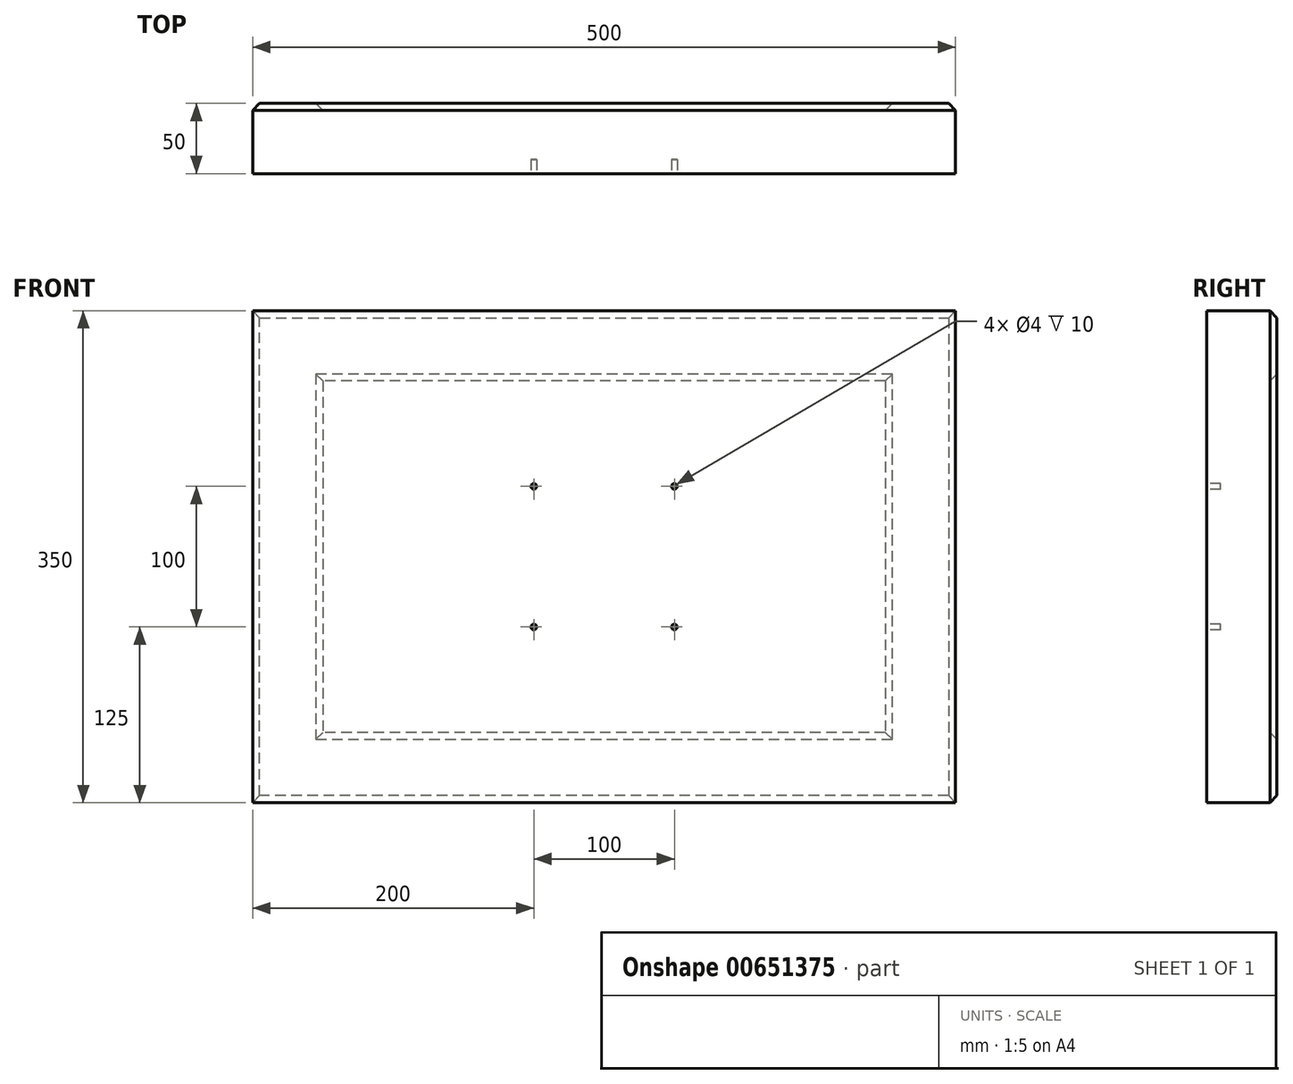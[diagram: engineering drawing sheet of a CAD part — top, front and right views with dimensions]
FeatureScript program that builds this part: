
annotation { "Feature Type Name" : "Feature", "Feature Type Description" : "" }
export const myFeature = defineFeature(function(context is Context, id is Id, definition is map)
    precondition{}
    {
        {
            var Q0;
            Q0=qCreatedBy(makeId("Front.planeOp"),FACE);
            var sketch = newSketch(context, id + "F0", { "sketchPlane" : qUnion([Q0])});
            skLineSegment(sketch, "E0.bottom", {"start": v(250, 175) * mm, "end": v(-250, 175) * mm});
            skLineSegment(sketch, "E0.top", {"start": v(250, -175) * mm, "end": v(-250, -175) * mm});
            skLineSegment(sketch, "E0.left", {"start": v(250, 175) * mm, "end": v(250, -175) * mm});
            skLineSegment(sketch, "E0.right", {"start": v(-250, 175) * mm, "end": v(-250, -175) * mm});
            skPoint(sketch, "E0.middle", {"position": v(0, 0) * mm});
            skSolve(sketch);
        }
        {
            var Q0;
            Q0 = qSketchRegion(id + "F0", true);
            extrude(context, id + "F1", {"entities" : qUnion([Q0]), "depth" : 50 * mm, "offsetDistance" : 25 * mm});
        }
        {
            var Q0;
            Q0=makeQuery(id+"F1.opExtrude","CAP_FACE",FACE,{"disambiguationData":[OSD([sQuery(id+"F0.wireOp",EDGE,"E0.bottom"),sQuery(id+"F0.wireOp",EDGE,"E0.top"),sQuery(id+"F0.wireOp",EDGE,"E0.left"),sQuery(id+"F0.wireOp",EDGE,"E0.right")])],"isStart":false});
            var sketch = newSketch(context, id + "F2", { "sketchPlane" : qUnion([Q0])});
            skLineSegment(sketch, "E1.bottom", {"start": v(50, 50) * mm, "end": v(-50, 50) * mm, "construction": true});
            skLineSegment(sketch, "E1.top", {"start": v(50, -50) * mm, "end": v(-50, -50) * mm, "construction": true});
            skLineSegment(sketch, "E1.left", {"start": v(50, 50) * mm, "end": v(50, -50) * mm, "construction": true});
            skLineSegment(sketch, "E1.right", {"start": v(-50, 50) * mm, "end": v(-50, -50) * mm, "construction": true});
            skPoint(sketch, "E1.middle", {"position": v(0, 0) * mm});
            skCircle(sketch, "E2", {"center": v(-50, 50) * mm, "radius": 2 * mm});
            skCircle(sketch, "E3", {"center": v(50, 50) * mm, "radius": 2 * mm});
            skCircle(sketch, "E4", {"center": v(50, -50) * mm, "radius": 2 * mm});
            skCircle(sketch, "E5", {"center": v(-50, -50) * mm, "radius": 2 * mm});
            skSolve(sketch);
        }
        {
            var Q0;
            Q0 = qSketchRegion(id + "F2", true);
            extrude(context, id + "F3", {"entities" : qUnion([Q0]), "operationType" : NewBodyOperationType.REMOVE, "oppositeDirection" : true, "depth" : 10 * mm, "offsetDistance" : 25 * mm});
        }
        {
            var Q0;
            Q0=makeQuery(id+"F1.opExtrude","CAP_FACE",FACE,{"disambiguationData":[OSD([sQuery(id+"F0.wireOp",EDGE,"E0.bottom"),sQuery(id+"F0.wireOp",EDGE,"E0.top"),sQuery(id+"F0.wireOp",EDGE,"E0.left"),sQuery(id+"F0.wireOp",EDGE,"E0.right")])],"isStart":true});
            var sketch = newSketch(context, id + "F4", { "sketchPlane" : qUnion([Q0])});
            skLineSegment(sketch, "E6.bottom", {"start": v(-200, 125) * mm, "end": v(200, 125) * mm});
            skLineSegment(sketch, "E6.top", {"start": v(-200, -125) * mm, "end": v(200, -125) * mm});
            skLineSegment(sketch, "E6.left", {"start": v(-200, 125) * mm, "end": v(-200, -125) * mm});
            skLineSegment(sketch, "E6.right", {"start": v(200, 125) * mm, "end": v(200, -125) * mm});
            skPoint(sketch, "E6.middle", {"position": v(0, 0) * mm});
            skSolve(sketch);
        }
        {
            var Q0;
            Q0 = qSketchRegion(id + "F4", true);
            extrude(context, id + "F5", {"entities" : qUnion([Q0]), "operationType" : NewBodyOperationType.REMOVE, "oppositeDirection" : true, "depth" : 5 * mm, "offsetDistance" : 25 * mm});
        }
        {
            var Q0;
            Q0=makeQuery(id+"F1.opExtrude","CAP_FACE",FACE,{"disambiguationData":[OSD([sQuery(id+"F0.wireOp",EDGE,"E0.bottom"),sQuery(id+"F0.wireOp",EDGE,"E0.top"),sQuery(id+"F0.wireOp",EDGE,"E0.left"),sQuery(id+"F0.wireOp",EDGE,"E0.right")])],"isStart":true});
            chamfer(context, id + "F6", {"entities" : qUnion([Q0]), "width" : 5 * mm, "tangentPropagation" : true});
        }
    });
